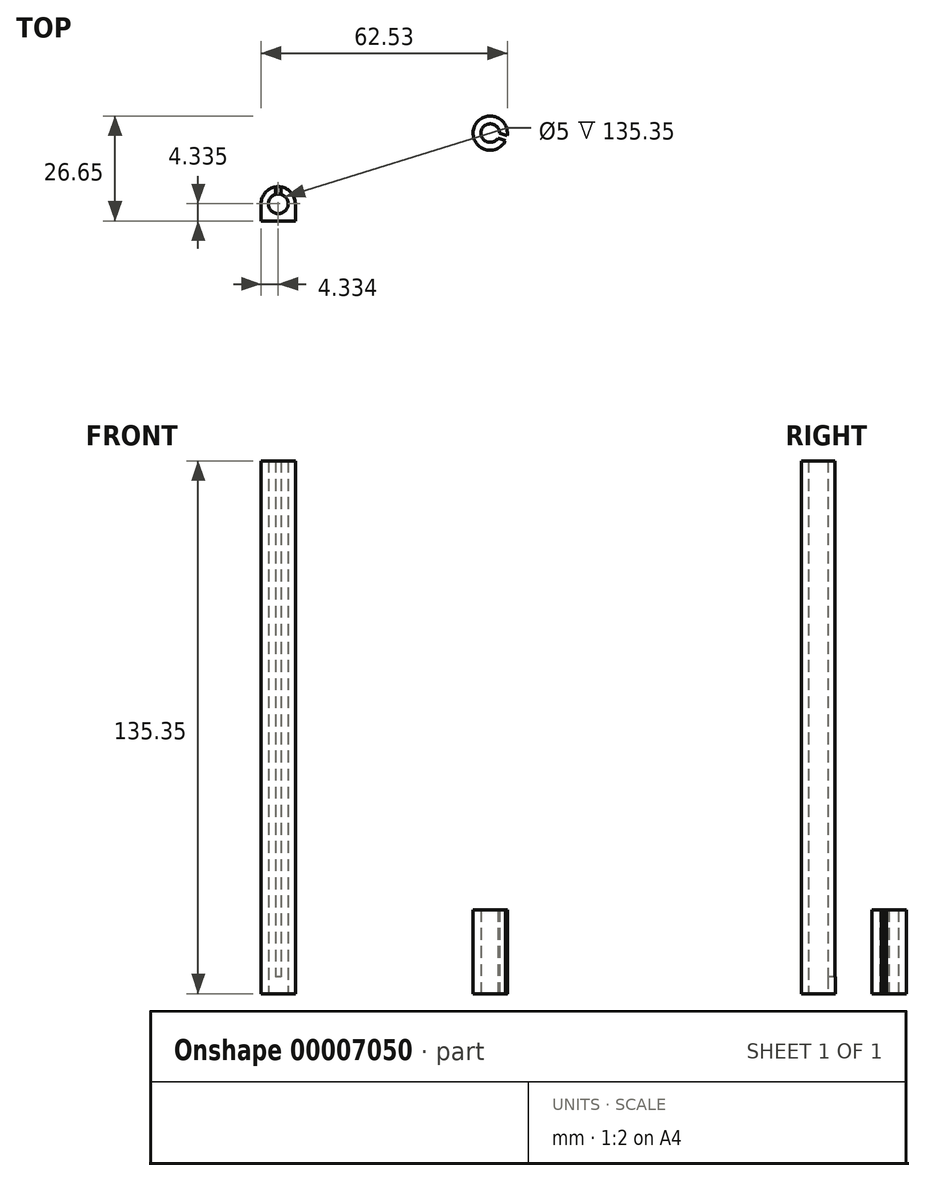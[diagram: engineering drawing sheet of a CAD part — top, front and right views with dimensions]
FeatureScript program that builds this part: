
annotation { "Feature Type Name" : "Feature", "Feature Type Description" : "" }
export const myFeature = defineFeature(function(context is Context, id is Id, definition is map)
    precondition{}
    {
        {
            var Q0;
            Q0=qCreatedBy(makeId("Top.planeOp"),FACE);
            var sketch = newSketch(context, id + "F0", { "sketchPlane" : qUnion([Q0])});
            skCircle(sketch, "E0", {"center": v(20.26, 38.85) * mm, "radius": 2.35 * mm});
            skCircle(sketch, "E1", {"center": v(20.26, 38.85) * mm, "radius": 4.35 * mm});
            skLineSegment(sketch, "E2", {"start": v(22.52, 38.19) * mm, "end": v(24.44, 37.63) * mm});
            skLineSegment(sketch, "E3", {"start": v(24.16, 36.9) * mm, "end": v(24.56, 38.19) * mm});
            skLineSegment(sketch, "E4", {"start": v(24.16, 36.9) * mm, "end": v(22.2, 37.53) * mm});
            skLineSegment(sketch, "E5", {"start": v(24.56, 38.19) * mm, "end": v(22.61, 38.8) * mm});
            skSolve(sketch);
        }
        {
            var Q0;
            {var subQ1=sQuery(id+"F0.wireOp",EDGE,"E4");Q0=makeQuery(id+"F0.imprint","IMPRINT",FACE,{"disambiguationData":[TD([[makeQuery(id+"F0.imprint","IMPRINT",EDGE,{"derivedFrom":subQ1}),1.0]])]});}
            extrude(context, id + "F1", {"entities" : qUnion([Q0]), "depth" : 21.3 * mm});
        }
        {
            var Q0;
            Q0=qCreatedBy(makeId("Top.planeOp"),FACE);
            var sketch = newSketch(context, id + "F2", { "sketchPlane" : qUnion([Q0])});
            skCircle(sketch, "E6", {"center": v(-33.59, 20.88) * mm, "radius": 2.5 * mm});
            skCircle(sketch, "E7", {"center": v(-33.59, 20.88) * mm, "radius": 4.33 * mm});
            skLineSegment(sketch, "E8", {"start": v(-33.59, 20.88) * mm, "end": v(-41.16, 20.88) * mm, "construction": true});
            skLineSegment(sketch, "E9", {"start": v(-41.16, 20.88) * mm, "end": v(-37.92, 20.88) * mm, "construction": true});
            skLineSegment(sketch, "E10", {"start": v(-37.92, 20.88) * mm, "end": v(-37.92, 14.7) * mm, "construction": true});
            skLineSegment(sketch, "E11", {"start": v(-33.59, 20.88) * mm, "end": v(-33.59, 16.55) * mm, "construction": true});
            skLineSegment(sketch, "E12", {"start": v(-33.59, 16.55) * mm, "end": v(-41.55, 16.55) * mm, "construction": true});
            skLineSegment(sketch, "E13", {"start": v(-37.92, 20.88) * mm, "end": v(-37.92, 16.55) * mm});
            skLineSegment(sketch, "E14", {"start": v(-37.92, 16.55) * mm, "end": v(-33.59, 16.55) * mm});
            skLineSegment(sketch, "E15.MirrorCS", {"start": v(-29.26, 20.88) * mm, "end": v(-29.26, 16.55) * mm});
            skLineSegment(sketch, "E16.MirrorCS", {"start": v(-29.26, 16.55) * mm, "end": v(-33.59, 16.55) * mm});
            skSolve(sketch);
        }
        {
            var Q0;
            Q0=makeQuery(id+"F2.imprint","IMPRINT",FACE,{"disambiguationData":[TD([[makeQuery(id+"F2.imprint","IMPRINT",EDGE,{"derivedFrom":sQuery(id+"F2.wireOp",EDGE,"E6")}),-1.0]])]});
            var Q1;
            {var subQ1=sQuery(id+"F2.wireOp",EDGE,"E13");Q1=makeQuery(id+"F2.imprint","IMPRINT",FACE,{"disambiguationData":[TD([[makeQuery(id+"F2.imprint","IMPRINT",EDGE,{"derivedFrom":subQ1}),1.0]])]});}
            var Q2;
            {var subQ1=sQuery(id+"F2.wireOp",EDGE,"E15.MirrorCS");Q2=makeQuery(id+"F2.imprint","IMPRINT",FACE,{"disambiguationData":[TD([[makeQuery(id+"F2.imprint","IMPRINT",EDGE,{"derivedFrom":subQ1}),-1.0]])]});}
            extrude(context, id + "F3", {"entities" : qUnion([Q0, Q1, Q2]), "depth" : 4.25 * mm});
        }
        {
            var Q0;
            Q0=makeQuery(id+"F3.opExtrude","CAP_FACE",FACE,{"disambiguationData":[OSD([sQuery(id+"F2.wireOp",EDGE,"E6"),sQuery(id+"F2.wireOp",EDGE,"E7")])],"isStart":false});
            var sketch = newSketch(context, id + "F4", { "sketchPlane" : qUnion([Q0])});
            skLineSegment(sketch, "E17", {"start": v(-33.59, 20.88) * mm, "end": v(-33.59, 28.06) * mm, "construction": true});
            skCircle(sketch, "E18", {"center": v(-33.59, 28.06) * mm, "radius": 0.71 * mm, "construction": true});
            skLineSegment(sketch, "E19", {"start": v(-33.59, 28.06) * mm, "end": v(-34.3, 28.06) * mm, "construction": true});
            skLineSegment(sketch, "E20", {"start": v(-34.3, 28.06) * mm, "end": v(-34.3, 22.28) * mm, "construction": true});
            skLineSegment(sketch, "E21", {"start": v(-34.3, 25.16) * mm, "end": v(-34.3, 23.28) * mm});
            skLineSegment(sketch, "E22.MirrorCS", {"start": v(-32.88, 25.16) * mm, "end": v(-32.88, 23.28) * mm});
            skSolve(sketch);
        }
        {
            var Q0;
            {var subQ3=sQuery(id+"F4.wireOp",EDGE,"E21");Q0=makeQuery(id+"F4.imprint","IMPRINT",FACE,{"disambiguationData":[TD([[makeQuery(id+"F4.imprint","IMPRINT",EDGE,{"derivedFrom":subQ3}),-1.0]])]});}
            extrude(context, id + "F5", {"entities" : qUnion([Q0]), "operationType" : NewBodyOperationType.ADD, "depth" : 26.6 * mm});
        }
        {
            var Q0;
            Q0=makeQuery(id+"F5.opExtrude","CAP_FACE",FACE,{"disambiguationData":[OSD([sQuery(id+"F2.wireOp",EDGE,"E6"),sQuery(id+"F2.wireOp",EDGE,"E7"),sQuery(id+"F2.wireOp",EDGE,"E13"),sQuery(id+"F2.wireOp",EDGE,"E14"),sQuery(id+"F2.wireOp",EDGE,"E15.MirrorCS"),sQuery(id+"F2.wireOp",EDGE,"E16.MirrorCS"),sQuery(id+"F4.wireOp",EDGE,"E21"),sQuery(id+"F4.wireOp",EDGE,"E22.MirrorCS")])],"isStart":false});
            extrude(context, id + "F6", {"entities" : qUnion([Q0]), "operationType" : NewBodyOperationType.ADD, "depth" : 104.5 * mm});
        }
    });
